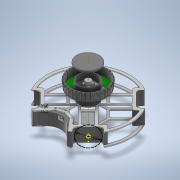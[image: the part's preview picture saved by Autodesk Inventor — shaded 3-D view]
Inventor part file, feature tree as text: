
AUTODESK INVENTOR PART (.ipt)
format: ipt  version: 2020 (Build 240168000, 168)  size: 2,160,640 bytes
history: native  units: mm
features: sketch x21, extrude x19, other x13, projected_geometry x4, pattern_circular x2, revolve x1
ambient origin geometry x8: Origin, YZ Plane, XZ Plane, XY Plane, X Axis, Y Axis, Z Axis, Center Point
bodies: Body1 (feature_tree)
feature tree (60):
  other  "Твердое тело1"
  other  "bottom_frame"
  other  "motowheels"
  extrude  "catcher"  Depth=88.0mm
  sketch  "Эскиз4"
  extrude  "Выдавливание2"  Depth=7.0mm
  extrude  "Выдавливание3"  Depth=5.0mm
  extrude  "Выдавливание21"  Depth=7.0mm
  other  "РабПлоскость1"
  extrude  "Выдавливание6"  Depth=5.0mm
  sketch  "Эскиз8"
  other  "РабПлоскость2"
  sketch  "Эскиз11"
  sketch  "Эскиз12"
  other  "РабПлоскость3"
  sketch  "Эскиз18"
  sketch  "Эскиз19"
  extrude  "Выдавливание15"  Depth=7.0mm
  extrude  "Выдавливание16"  Depth=5.0mm
  other  "РабПлоскость7"
  sketch  "Эскиз22"
  other  "РабПлоскость9"
  sketch  "Эскиз25"
  other  "РабПлоскость10"
  revolve  "Вращение2"
  sketch  "Эскиз29"
  extrude  "Выдавливание20"  Depth=5.1mm
  pattern_circular  "Круговой массив3"  Count=3  [1 undecoded]
  other  "РабПлоскость11"
  extrude  "Выдавливание22"  Depth=7.5mm
  other  "upper_frame"
  sketch  "Эскиз33"
  extrude  "Выдавливание23"  Depth=11.2mm
  sketch  "Эскиз34"
  other  "РабПлоскость12"
  extrude  "Выдавливание24"  Depth=20.5mm
  sketch  "Эскиз36"
  extrude  "Выдавливание25"  Depth=7.0mm TaperAngle=0.0deg
  extrude  "Выдавливание26"  Depth=4.0mm TaperAngle=0.0deg
  extrude  "Выдавливание27"  Depth=7.6mm
  pattern_circular  "Круговой массив4"  [2 undecoded]
  sketch  "Эскиз38"
  extrude  "Выдавливание28"  Depth=10.0mm
  extrude  "Выдавливание29"  Depth=15.0mm
  extrude  "Выдавливание30"  Depth=20.0mm TaperAngle=0.0deg
  sketch  "Эскиз40"
  other  "РабПлоскость13"
  extrude  "Выдавливание32"  Depth=3.0mm
  extrude  "Выдавливание33"  Depth=6.0mm
  sketch  "Эскиз7"
  projected_geometry  "Спроецированная петля1"
  sketch  "Эскиз26"
  projected_geometry  "Спроецированная петля2"
  sketch  "Эскиз30"
  projected_geometry  "Спроецированная петля3"
  projected_geometry  "Спроецированная петля4"
  sketch  "Эскиз35"
  sketch  "Эскиз37"
  sketch  "Эскиз39"
  sketch  "Эскиз41"
note: 3 required parameter values undecoded (feature->parameter linkage not recoverable at this tier; creation-order binding heuristic only, values carry confidence <= 0.55)
